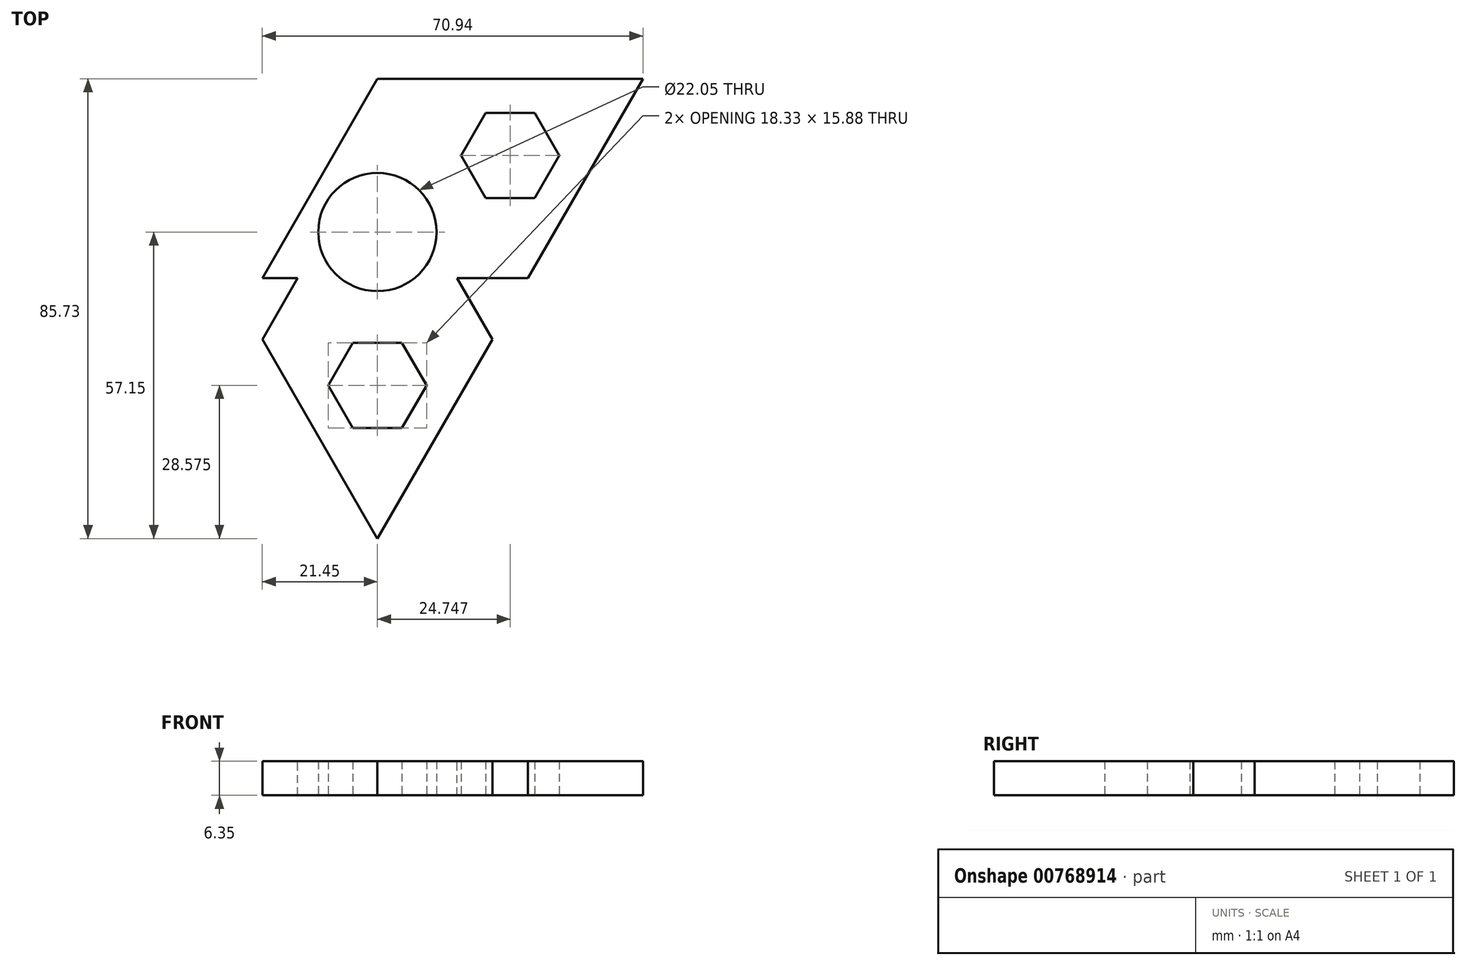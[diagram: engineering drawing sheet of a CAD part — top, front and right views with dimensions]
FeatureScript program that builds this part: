
annotation { "Feature Type Name" : "Feature", "Feature Type Description" : "" }
export const myFeature = defineFeature(function(context is Context, id is Id, definition is map)
    precondition{}
    {
        {
            var Q0;
            Q0=qCreatedBy(makeId("Top.planeOp"),FACE);
            var sketch = newSketch(context, id + "F0", { "sketchPlane" : qUnion([Q0])});
            skCircle(sketch, "E0", {"center": v(0, 0) * mm, "radius": 11.02 * mm});
            skCircle(sketch, "E1.cCircle", {"center": v(0, 0) * mm, "radius": 14.29 * mm, "construction": true});
            skLineSegment(sketch, "E1.0", {"start": v(24.75, -14.29) * mm, "end": v(-24.75, -14.29) * mm});
            skLineSegment(sketch, "E1.1", {"start": v(-24.75, -14.29) * mm, "end": v(0, 28.58) * mm});
            skLineSegment(sketch, "E1.2", {"start": v(0, 28.58) * mm, "end": v(24.75, -14.29) * mm});
            skPoint(sketch, "E1.0.midPoint", {"position": v(0, -14.29) * mm});
            skCircle(sketch, "E2.cCircle", {"center": v(-24.75, 14.29) * mm, "radius": 14.29 * mm, "construction": true});
            skLineSegment(sketch, "E2.0", {"start": v(0, 28.58) * mm, "end": v(-24.75, -14.29) * mm});
            skLineSegment(sketch, "E2.1", {"start": v(-24.75, -14.29) * mm, "end": v(-49.5, 28.58) * mm});
            skLineSegment(sketch, "E2.2", {"start": v(-49.5, 28.58) * mm, "end": v(0, 28.57) * mm});
            skPoint(sketch, "E2.0.midPoint", {"position": v(-12.37, 7.14) * mm});
            skLineSegment(sketch, "E3.1.0", {"start": v(0, -57.15) * mm, "end": v(-24.75, -14.29) * mm});
            skLineSegment(sketch, "E3.1.1", {"start": v(24.75, -14.29) * mm, "end": v(0, -57.15) * mm});
            skLineSegment(sketch, "E3.2.0", {"start": v(49.5, 28.57) * mm, "end": v(24.75, -14.29) * mm});
            skLineSegment(sketch, "E3.2.1", {"start": v(0, 28.58) * mm, "end": v(49.5, 28.58) * mm});
            skCircle(sketch, "E4.cCircle", {"center": v(-24.75, 14.29) * mm, "radius": 7.94 * mm, "construction": true});
            skLineSegment(sketch, "E4.0", {"start": v(-15.58, 14.29) * mm, "end": v(-20.16, 6.35) * mm});
            skLineSegment(sketch, "E4.1", {"start": v(-20.16, 6.35) * mm, "end": v(-29.33, 6.35) * mm});
            skLineSegment(sketch, "E4.2", {"start": v(-29.33, 6.35) * mm, "end": v(-33.91, 14.29) * mm});
            skLineSegment(sketch, "E4.3", {"start": v(-33.91, 14.29) * mm, "end": v(-29.33, 22.22) * mm});
            skLineSegment(sketch, "E4.4", {"start": v(-29.33, 22.22) * mm, "end": v(-20.16, 22.22) * mm});
            skLineSegment(sketch, "E4.5", {"start": v(-20.16, 22.22) * mm, "end": v(-15.58, 14.29) * mm});
            skPoint(sketch, "E4.0.midPoint", {"position": v(-17.87, 10.32) * mm});
            skLineSegment(sketch, "E5.1.0", {"start": v(-9.17, -28.58) * mm, "end": v(-4.58, -20.64) * mm});
            skLineSegment(sketch, "E5.1.1", {"start": v(-4.58, -36.51) * mm, "end": v(-9.17, -28.58) * mm});
            skLineSegment(sketch, "E5.1.2", {"start": v(4.58, -36.51) * mm, "end": v(-4.58, -36.51) * mm});
            skLineSegment(sketch, "E5.1.3", {"start": v(9.17, -28.58) * mm, "end": v(4.58, -36.51) * mm});
            skLineSegment(sketch, "E5.1.4", {"start": v(4.58, -20.64) * mm, "end": v(9.17, -28.58) * mm});
            skLineSegment(sketch, "E5.1.5", {"start": v(-4.58, -20.64) * mm, "end": v(4.58, -20.64) * mm});
            skLineSegment(sketch, "E5.2.0", {"start": v(29.33, 6.35) * mm, "end": v(20.16, 6.35) * mm});
            skLineSegment(sketch, "E5.2.1", {"start": v(33.91, 14.29) * mm, "end": v(29.33, 6.35) * mm});
            skLineSegment(sketch, "E5.2.2", {"start": v(29.33, 22.22) * mm, "end": v(33.91, 14.29) * mm});
            skLineSegment(sketch, "E5.2.3", {"start": v(20.16, 22.22) * mm, "end": v(29.33, 22.22) * mm});
            skLineSegment(sketch, "E5.2.4", {"start": v(15.58, 14.29) * mm, "end": v(20.16, 22.22) * mm});
            skLineSegment(sketch, "E5.2.5", {"start": v(20.16, 6.35) * mm, "end": v(15.58, 14.29) * mm});
            skSolve(sketch);
        }
        {
            var Q0;
            Q0=makeQuery(id+"F0.imprint","IMPRINT",FACE,{"disambiguationData":[TD([[makeQuery(id+"F0.imprint","IMPRINT",EDGE,{"derivedFrom":sQuery(id+"F0.wireOp",EDGE,"E2.0")}),-1.0]])]});
            var Q1;
            Q1=makeQuery(id+"F0.imprint","IMPRINT",FACE,{"disambiguationData":[TD([[makeQuery(id+"F0.imprint","IMPRINT",EDGE,{"derivedFrom":sQuery(id+"F0.wireOp",EDGE,"E0")}),-1.0]])]});
            var Q2;
            Q2=makeQuery(id+"F0.imprint","IMPRINT",FACE,{"disambiguationData":[TD([[makeQuery(id+"F0.imprint","IMPRINT",EDGE,{"derivedFrom":sQuery(id+"F0.wireOp",EDGE,"E1.2")}),1.0]])]});
            var Q3;
            Q3=makeQuery(id+"F0.imprint","IMPRINT",FACE,{"disambiguationData":[TD([[makeQuery(id+"F0.imprint","IMPRINT",EDGE,{"derivedFrom":sQuery(id+"F0.wireOp",EDGE,"E1.0")}),1.0]])]});
            extrude(context, id + "F1", {"entities" : qUnion([Q0, Q1, Q2, Q3]), "depth" : 6.35 * mm, "offsetDistance" : 25.4 * mm});
        }
        {
            var Q0;
            Q0=makeQuery(id+"F1.opExtrude","CAP_FACE",FACE,{"disambiguationData":[OSD([sQuery(id+"F0.wireOp",EDGE,"E0"),sQuery(id+"F0.wireOp",EDGE,"E2.1"),sQuery(id+"F0.wireOp",EDGE,"E2.2"),sQuery(id+"F0.wireOp",EDGE,"E3.1.0"),sQuery(id+"F0.wireOp",EDGE,"E3.1.1"),sQuery(id+"F0.wireOp",EDGE,"E3.2.0"),sQuery(id+"F0.wireOp",EDGE,"E3.2.1"),sQuery(id+"F0.wireOp",EDGE,"E95LwEal-SG1h-VE3A-DFBR-adsU54bkwXvx"),sQuery(id+"F0.wireOp",EDGE,"9dbaaab3-d26d-4a4b-a971-b244d4a9bdfc.1.0"),sQuery(id+"F0.wireOp",EDGE,"9dbaaab3-d26d-4a4b-a971-b244d4a9bdfc.2.0")])],"isStart":false});
            var sketch = newSketch(context, id + "F2", { "sketchPlane" : qUnion([Q0])});
            skCircle(sketch, "E6.cCircle", {"center": v(0, 24.76) * mm, "radius": 3.81 * mm, "construction": true});
            skPoint(sketch, "E6.cCircle.centerSnap0", {"position": v(0, 28.57) * mm});
            skLineSegment(sketch, "E6.0", {"start": v(-6.6, 28.57) * mm, "end": v(6.6, 28.57) * mm});
            skLineSegment(sketch, "E6.1", {"start": v(6.6, 28.58) * mm, "end": v(0, 17.14) * mm});
            skLineSegment(sketch, "E6.2", {"start": v(0, 17.14) * mm, "end": v(-6.6, 28.57) * mm});
            skPoint(sketch, "E6.0.midPoint", {"position": v(0, 28.57) * mm});
            skLineSegment(sketch, "E7.1.0", {"start": v(-28.05, -8.57) * mm, "end": v(-14.85, -8.57) * mm});
            skLineSegment(sketch, "E7.1.1", {"start": v(-14.85, -8.57) * mm, "end": v(-21.45, -20) * mm});
            skLineSegment(sketch, "E7.2.0", {"start": v(21.45, -20) * mm, "end": v(14.85, -8.57) * mm});
            skLineSegment(sketch, "E7.2.1", {"start": v(14.85, -8.57) * mm, "end": v(28.05, -8.57) * mm});
            skPoint(sketch, "E7.center", {"position": v(0, 0) * mm});
            skSolve(sketch);
        }
        {
            var Q0;
            Q0=makeQuery(id+"F2.imprint","IMPRINT",FACE,{"disambiguationData":[TD([[makeQuery(id+"F2.imprint","IMPRINT",EDGE,{"derivedFrom":sQuery(id+"F2.wireOp",EDGE,"E6.0")}),-1.0]])]});
            var Q1;
            {var subQ0=sQuery(id+"F2.wireOp",EDGE,"E7.1.0");Q1=makeQuery(id+"F2.imprint","IMPRINT",FACE,{"disambiguationData":[TD([[makeQuery(id+"F2.imprint","IMPRINT",EDGE,{"derivedFrom":subQ0}),-1.0]])]});}
            var Q2;
            {var subQ0=sQuery(id+"F2.wireOp",EDGE,"E7.2.0");Q2=makeQuery(id+"F2.imprint","IMPRINT",FACE,{"disambiguationData":[TD([[makeQuery(id+"F2.imprint","IMPRINT",EDGE,{"derivedFrom":subQ0}),-1.0]])]});}
            extrude(context, id + "F3", {"entities" : qUnion([Q0, Q1, Q2]), "operationType" : NewBodyOperationType.REMOVE, "oppositeDirection" : true, "depth" : 6.35 * mm, "offsetDistance" : 25.4 * mm});
        }
    });
